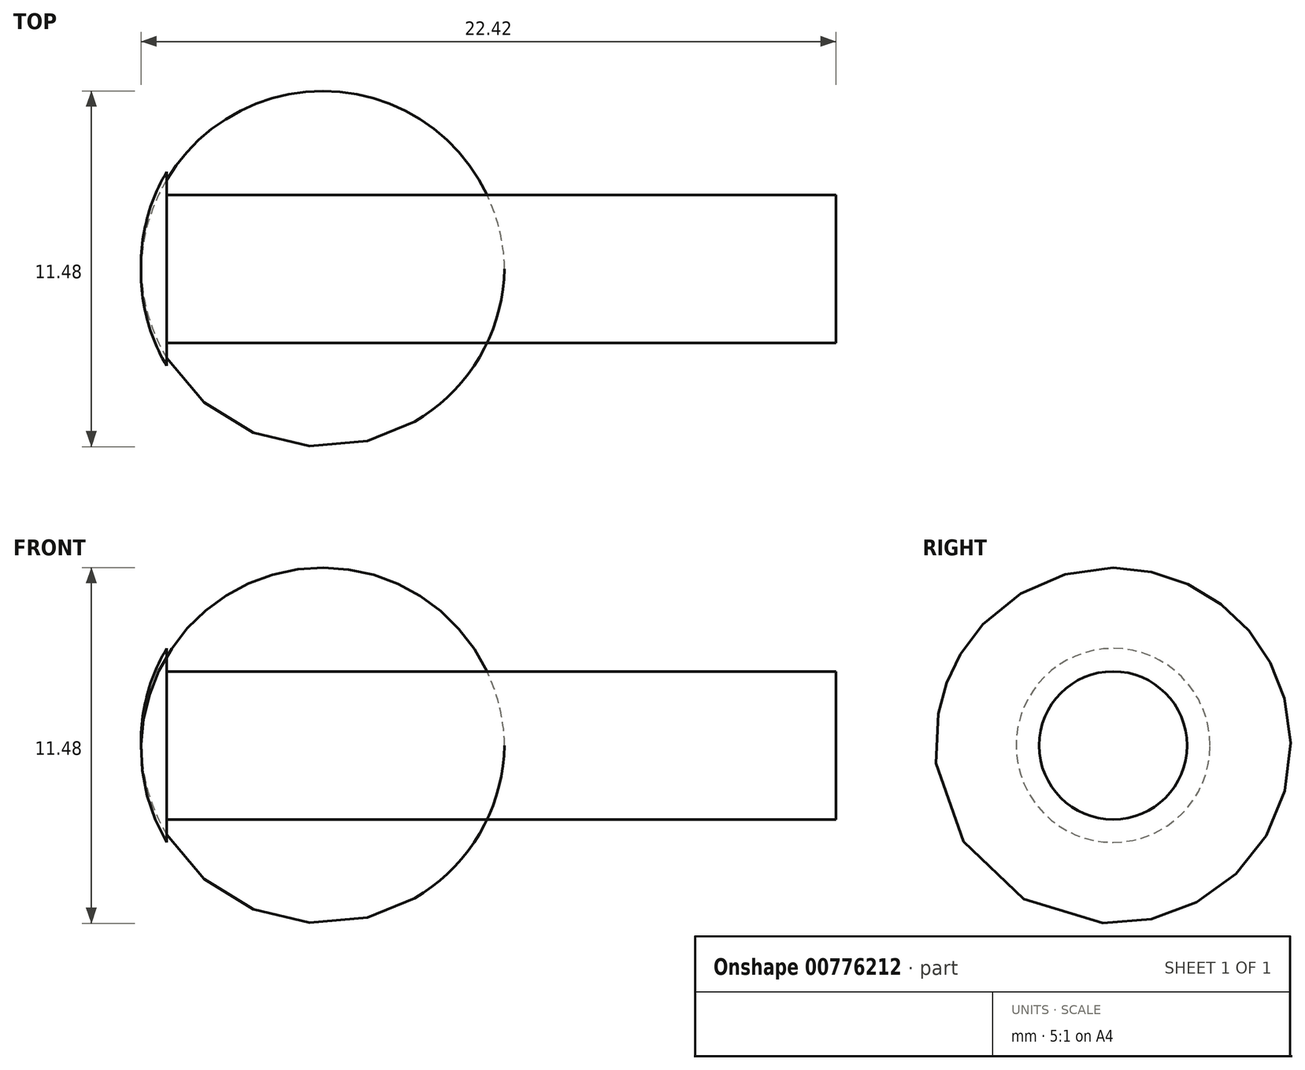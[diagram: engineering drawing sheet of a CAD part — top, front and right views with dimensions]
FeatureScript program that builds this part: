
annotation { "Feature Type Name" : "Feature", "Feature Type Description" : "" }
export const myFeature = defineFeature(function(context is Context, id is Id, definition is map)
    precondition{}
    {
        {
            var Q0;
            Q0=qCreatedBy(makeId("Right.planeOp"),FACE);
            var sketch = newSketch(context, id + "F0", { "sketchPlane" : qUnion([Q0])});
            skCircle(sketch, "E0", {"center": v(0, 0) * mm, "radius": 2.39 * mm});
            skSolve(sketch);
        }
        {
            var Q0;
            Q0 = qSketchRegion(id + "F0", true);
            extrude(context, id + "F1", {"entities" : qUnion([Q0]), "depth" : 21.59 * mm, "offsetDistance" : 25.4 * mm});
        }
        {
            var Q0;
            Q0=qCreatedBy(makeId("Top.planeOp"),FACE);
            var sketch = newSketch(context, id + "F2", { "sketchPlane" : qUnion([Q0])});
            skLineSegment(sketch, "E1", {"start": v(0, 0) * mm, "end": v(-3.96, 0) * mm, "construction": true});
            skLineSegment(sketch, "E2", {"start": v(0, 0) * mm, "end": v(0, -3.13) * mm});
            skLineSegment(sketch, "E3", {"start": v(0, 0) * mm, "end": v(-0.82, 0) * mm});
            skArc(sketch, "E4", {"start": v(-0.82, 0) * mm, "mid": v(-0.63, -1.62) * mm, "end": v(0, -3.13) * mm});
            skSolve(sketch);
        }
        {
            var Q0;
            Q0=makeQuery(id+"F2.imprint","IMPRINT",FACE,{"disambiguationData":[TD([[makeQuery(id+"F2.imprint","IMPRINT",EDGE,{"derivedFrom":sQuery(id+"F2.wireOp",EDGE,"E2")}),-1.0]])]});
            var Q1;
            Q1=sQuery(id+"F2.wireOp",EDGE,"E1");
            revolve(context, id + "F3", {"operationType" : NewBodyOperationType.ADD, "surfaceOperationType" : NewSurfaceOperationType.NEW, "entities" : qUnion([Q0]), "axis" : qUnion([Q1]), "revolveType" : RevolveType.FULL});
        }
    });
